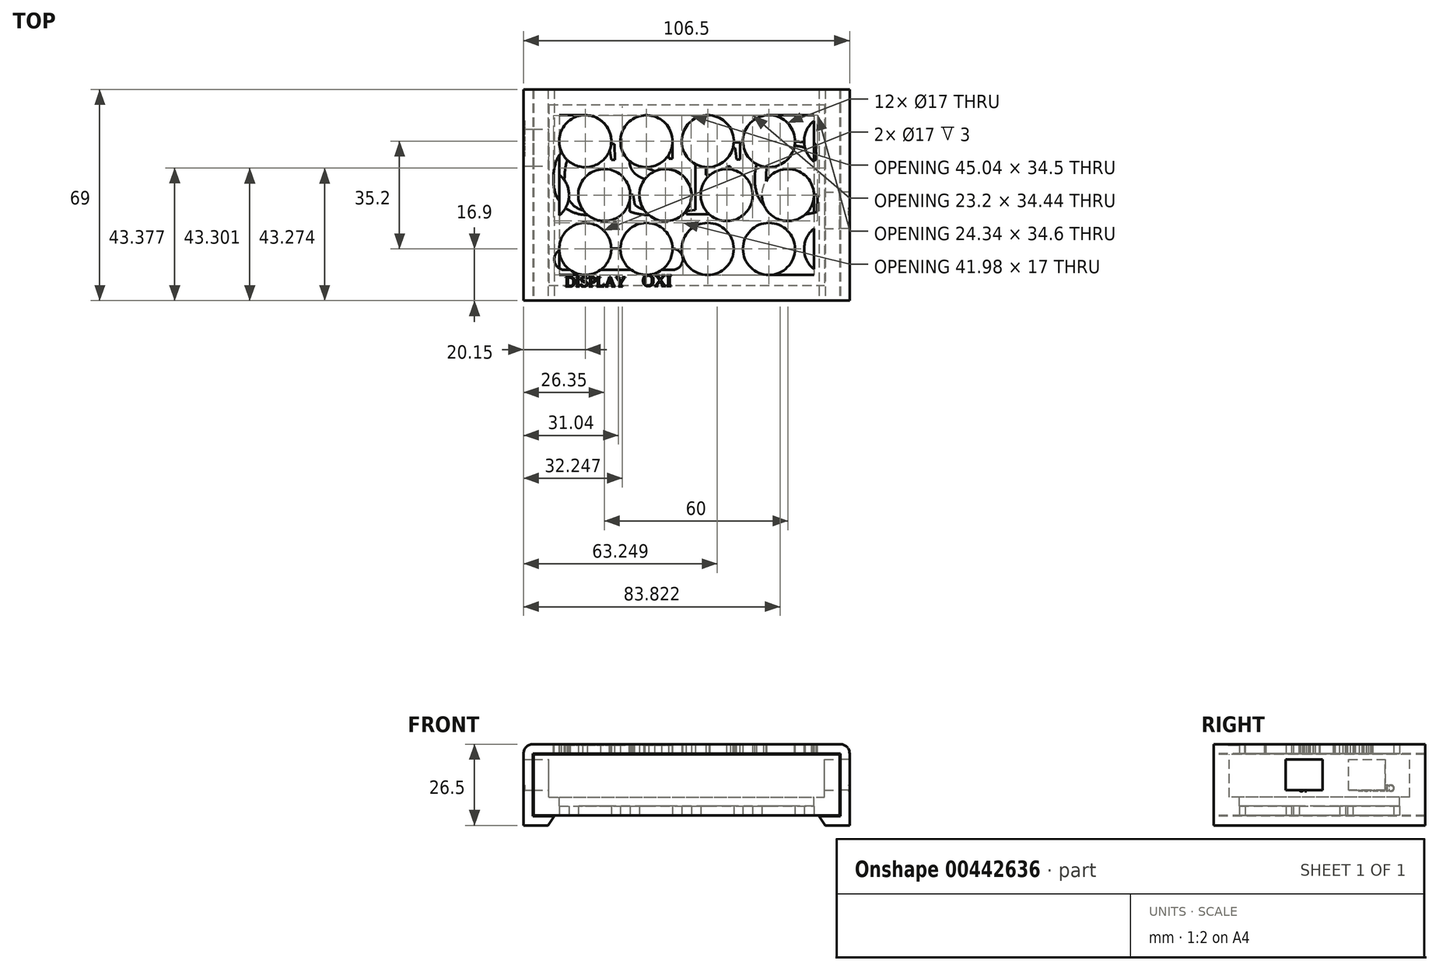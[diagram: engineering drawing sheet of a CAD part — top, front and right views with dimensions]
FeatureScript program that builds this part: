
annotation { "Feature Type Name" : "Feature", "Feature Type Description" : "" }
export const myFeature = defineFeature(function(context is Context, id is Id, definition is map)
    precondition{}
    {
        {
            var Q0;
            Q0=qCreatedBy(makeId("Top.planeOp"),FACE);
            var sketch = newSketch(context, id + "F0", { "sketchPlane" : qUnion([Q0])});
            skLineSegment(sketch, "E0.bottom", {"start": v(-50, 34.5) * mm, "end": v(50, 34.5) * mm});
            skLineSegment(sketch, "E0.top", {"start": v(-50, -34.5) * mm, "end": v(50, -34.5) * mm});
            skLineSegment(sketch, "E0.left", {"start": v(-50, 34.5) * mm, "end": v(-50, -34.5) * mm});
            skLineSegment(sketch, "E0.right", {"start": v(50, 34.5) * mm, "end": v(50, -34.5) * mm});
            skSolve(sketch);
        }
        {
            var Q0;
            Q0=qSketchRegion(id+"F0",true);
            extrude(context, id + "F1", {"entities" : qUnion([Q0]), "depth" : 20 * mm});
        }
        {
            var Q0;
            Q0=makeQuery(id+"F1.opExtrude","CAP_FACE",FACE,{"disambiguationData":[OSD([sQuery(id+"F0.wireOp",EDGE,"E0.bottom"),sQuery(id+"F0.wireOp",EDGE,"E0.top"),sQuery(id+"F0.wireOp",EDGE,"E0.left"),sQuery(id+"F0.wireOp",EDGE,"E0.right")])],"isStart":false});
            var sketch = newSketch(context, id + "F2", { "sketchPlane" : qUnion([Q0])});
            skLineSegment(sketch, "E1.bottom", {"start": v(-45, 29.5) * mm, "end": v(45, 29.5) * mm});
            skLineSegment(sketch, "E1.top", {"start": v(-45, -29.5) * mm, "end": v(45, -29.5) * mm});
            skLineSegment(sketch, "E1.left", {"start": v(-45, 29.5) * mm, "end": v(-45, -29.5) * mm});
            skLineSegment(sketch, "E1.right", {"start": v(45, 29.5) * mm, "end": v(45, -29.5) * mm});
            skSolve(sketch);
        }
        {
            var Q0;
            Q0=makeQuery(id+"F2.imprint","IMPRINT",FACE,{"disambiguationData":[TD([[makeQuery(id+"F2.imprint","IMPRINT",EDGE,{"derivedFrom":sQuery(id+"F2.wireOp",EDGE,"E1.bottom")}),-1.0]])]});
            extrude(context, id + "F3", {"entities" : qUnion([Q0]), "operationType" : NewBodyOperationType.REMOVE, "oppositeDirection" : true, "depth" : 14 * mm});
        }
        {
            var Q0;
            Q0=makeQuery(id+"F3.boolean.opBoolean","COPY",FACE,{"derivedFrom":makeQuery(id+"F3.opExtrude","CAP_FACE",FACE,{"disambiguationData":[OSD([sQuery(id+"F2.wireOp",EDGE,"E1.bottom"),sQuery(id+"F2.wireOp",EDGE,"E1.top"),sQuery(id+"F2.wireOp",EDGE,"E1.left"),sQuery(id+"F2.wireOp",EDGE,"E1.right")])],"isStart":false})});
            var sketch = newSketch(context, id + "F4", { "sketchPlane" : qUnion([Q0])});
            skLineSegment(sketch, "E2.bottom", {"start": v(-41.6, 26.1) * mm, "end": v(41.6, 26.1) * mm});
            skLineSegment(sketch, "E2.top", {"start": v(-41.6, -26.1) * mm, "end": v(41.6, -26.1) * mm});
            skLineSegment(sketch, "E2.left", {"start": v(-41.6, 26.1) * mm, "end": v(-41.6, -26.1) * mm});
            skLineSegment(sketch, "E2.right", {"start": v(41.6, 26.1) * mm, "end": v(41.6, -26.1) * mm});
            skSolve(sketch);
        }
        {
            var Q0;
            Q0=qSketchRegion(id+"F4",true);
            extrude(context, id + "F5", {"entities" : qUnion([Q0]), "operationType" : NewBodyOperationType.REMOVE, "oppositeDirection" : true, "depth" : 3 * mm});
        }
        {
            var Q0;
            Q0=makeQuery(id+"F1.opExtrude","SWEPT_FACE",FACE,{"disambiguationData":[OSD([sQuery(id+"F0.wireOp",EDGE,"E0.top")])]});
            cPlane(context, id + "F6", {"entities" : qUnion([Q0]), "cplaneType" : CPlaneType.OFFSET, "offset" : 0 * mm, "width" : 150 * mm, "height" : 150 * mm});
        }
        {
            var Q0;
            Q0=qCreatedBy(id+"F6.planeOp",FACE);
            var sketch = newSketch(context, id + "F7", { "sketchPlane" : qUnion([Q0])});
            skLineSegment(sketch, "E3.0.0", {"start": v(-50, 0) * mm, "end": v(50, 0) * mm});
            skLineSegment(sketch, "E3.0.1", {"start": v(50, 0) * mm, "end": v(50, 20) * mm});
            skLineSegment(sketch, "E3.0.2", {"start": v(50, 20) * mm, "end": v(-50, 20) * mm});
            skLineSegment(sketch, "E3.0.3", {"start": v(-50, 20) * mm, "end": v(-50, 0) * mm});
            skLineSegment(sketch, "E4", {"start": v(0, 23.25) * mm, "end": v(-53.25, 23.25) * mm});
            skLineSegment(sketch, "E5", {"start": v(-53.25, 23.25) * mm, "end": v(-53.25, -3.25) * mm});
            skLineSegment(sketch, "E6", {"start": v(-53.25, -3.25) * mm, "end": v(-45.25, -3.25) * mm});
            skLineSegment(sketch, "E7", {"start": v(-45.25, -3.25) * mm, "end": v(-43.25, -0.25) * mm});
            skLineSegment(sketch, "E8", {"start": v(-43.25, -0.25) * mm, "end": v(-50.25, -0.25) * mm});
            skLineSegment(sketch, "E9", {"start": v(-50.25, -0.25) * mm, "end": v(-50.25, 20.25) * mm});
            skLineSegment(sketch, "E10", {"start": v(-50.25, 20.25) * mm, "end": v(0, 20.25) * mm});
            skLineSegment(sketch, "E11", {"start": v(0, 20.25) * mm, "end": v(0, 23.25) * mm});
            skLineSegment(sketch, "E12.MirrorCS", {"start": v(0, 23.25) * mm, "end": v(53.25, 23.25) * mm});
            skLineSegment(sketch, "E13.MirrorCS", {"start": v(50.25, 20.25) * mm, "end": v(0, 20.25) * mm});
            skLineSegment(sketch, "E14.MirrorCS", {"start": v(53.25, 23.25) * mm, "end": v(53.25, -3.25) * mm});
            skLineSegment(sketch, "E15.MirrorCS", {"start": v(50.25, -0.25) * mm, "end": v(50.25, 20.25) * mm});
            skLineSegment(sketch, "E16.MirrorCS", {"start": v(53.25, -3.25) * mm, "end": v(45.25, -3.25) * mm});
            skLineSegment(sketch, "E17.MirrorCS", {"start": v(45.25, -3.25) * mm, "end": v(43.25, -0.25) * mm});
            skLineSegment(sketch, "E18.MirrorCS", {"start": v(43.25, -0.25) * mm, "end": v(50.25, -0.25) * mm});
            skSolve(sketch);
        }
        {
            var Q0;
            Q0=makeQuery(id+"F7.imprint","IMPRINT",FACE,{"disambiguationData":[TD([[makeQuery(id+"F7.imprint","IMPRINT",EDGE,{"derivedFrom":sQuery(id+"F7.wireOp",EDGE,"E4")}),1.0]])]});
            var Q1;
            Q1=makeQuery(id+"F7.imprint","IMPRINT",FACE,{"disambiguationData":[TD([[makeQuery(id+"F7.imprint","IMPRINT",EDGE,{"derivedFrom":sQuery(id+"F7.wireOp",EDGE,"E11")}),-1.0]])]});
            extrude(context, id + "F8", {"entities" : qUnion([Q0, Q1]), "oppositeDirection" : true, "depth" : 69 * mm});
        }
        {
            var Q0;
            Q0=makeQuery(id+"F8.opExtrude","SWEPT_FACE",FACE,{"disambiguationData":[OSD([sQuery(id+"F7.wireOp",EDGE,"E4"),sQuery(id+"F7.wireOp",EDGE,"E12.MirrorCS")])]});
            var sketch = newSketch(context, id + "F9", { "sketchPlane" : qUnion([Q0])});
            skLineSegment(sketch, "E19.bottom", {"start": v(-39.7, -17.5) * mm, "end": v(-19.7, -17.5) * mm});
            skLineSegment(sketch, "E19.top", {"start": v(-39.7, -24.5) * mm, "end": v(-19.7, -24.5) * mm});
            skLineSegment(sketch, "E19.left", {"start": v(-39.7, -17.5) * mm, "end": v(-39.7, -24.5) * mm});
            skArc(sketch, "E20", {"start": v(-39.7, -17.5) * mm, "mid": v(-43.2, -21) * mm, "end": v(-39.7, -24.5) * mm});
            skLineSegment(sketch, "E21", {"start": v(-19.7, -17.5) * mm, "end": v(-4.03, -17.5) * mm, "construction": true});
            skLineSegment(sketch, "E22", {"start": v(-19.7, -24.5) * mm, "end": v(-4.03, -24.5) * mm, "construction": true});
            skLineSegment(sketch, "E23.bottom", {"start": v(-14.72, -17.5) * mm, "end": v(-4.72, -17.5) * mm});
            skLineSegment(sketch, "E23.top", {"start": v(-14.45, -24.5) * mm, "end": v(-4.72, -24.5) * mm});
            skLineSegment(sketch, "E23.right", {"start": v(-4.72, -17.5) * mm, "end": v(-4.72, -24.5) * mm});
            skArc(sketch, "E24", {"start": v(-4.72, -24.5) * mm, "mid": v(-1.22, -21) * mm, "end": v(-4.72, -17.5) * mm});
            skText(sketch, "E25", { "text": "DISPLAY", "fontName": "Tinos-Regular.ttf"});
            skText(sketch, "E26", { "text": "OXI", "fontName": "Tinos-Regular.ttf"});
            skLineSegment(sketch, "E27", {"start": v(-19.7, -17.5) * mm, "end": v(-14.45, -17.5) * mm});
            skLineSegment(sketch, "E28", {"start": v(-19.7, -24.5) * mm, "end": v(-14.45, -24.5) * mm});
            const initialGuessF9  = {"E25": [-0.0397, -0.02988, 1, 0, 0.00338], "E26": [-0.01445, -0.02973, 1, 0, 0.00388]};
            skSetInitialGuess(sketch, initialGuessF9);
            skSolve(sketch);
        }
        {
            var Q0;
            Q0=makeQuery(id+"F9.imprint","IMPRINT",FACE,{"disambiguationData":[TD([[makeQuery(id+"F9.imprint","IMPRINT",EDGE,{"derivedFrom":sQuery(id+"F9.wireOp",EDGE,"E23.bottom")}),-1.0]])]});
            var Q1;
            Q1=makeQuery(id+"F9.imprint","IMPRINT",FACE,{"disambiguationData":[TD([[makeQuery(id+"F9.imprint","IMPRINT",EDGE,{"derivedFrom":sQuery(id+"F9.wireOp",EDGE,"E23.left")}),-1.0]])]});
            var Q2;
            Q2=makeQuery(id+"F9.imprint","IMPRINT",FACE,{"disambiguationData":[TD([[makeQuery(id+"F9.imprint","IMPRINT",EDGE,{"derivedFrom":sQuery(id+"F9.wireOp",EDGE,"E23.right")}),1.0]])]});
            var Q3;
            Q3=makeQuery(id+"F9.imprint","IMPRINT",FACE,{"disambiguationData":[TD([[makeQuery(id+"F9.imprint","IMPRINT",EDGE,{"derivedFrom":sQuery(id+"F9.wireOp",EDGE,"E19.right")}),1.0]])]});
            var Q4;
            Q4=makeQuery(id+"F9.imprint","IMPRINT",FACE,{"disambiguationData":[TD([[makeQuery(id+"F9.imprint","IMPRINT",EDGE,{"derivedFrom":sQuery(id+"F9.wireOp",EDGE,"E19.bottom")}),-1.0]])]});
            var Q5;
            Q5=makeQuery(id+"F9.imprint","IMPRINT",FACE,{"disambiguationData":[TD([[makeQuery(id+"F9.imprint","IMPRINT",EDGE,{"derivedFrom":sQuery(id+"F9.wireOp",EDGE,"E19.left")}),-1.0]])]});
            extrude(context, id + "F10", {"entities" : qUnion([Q0, Q1, Q2, Q3, Q4, Q5]), "operationType" : NewBodyOperationType.REMOVE, "oppositeDirection" : true, "depth" : 5 * mm});
        }
        {
            var Q0;
            Q0=makeQuery(id+"F1.opExtrude","CAP_FACE",FACE,{"disambiguationData":[OSD([sQuery(id+"F0.wireOp",EDGE,"E0.bottom"),sQuery(id+"F0.wireOp",EDGE,"E0.top"),sQuery(id+"F0.wireOp",EDGE,"E0.left"),sQuery(id+"F0.wireOp",EDGE,"E0.right")])],"isStart":true});
            var sketch = newSketch(context, id + "F11", { "sketchPlane" : qUnion([Q0])});
            skLineSegment(sketch, "E29.0", {"start": v(-41.6, -26.1) * mm, "end": v(-41.6, 26.1) * mm});
            skLineSegment(sketch, "E30.0", {"start": v(-41.6, -26.1) * mm, "end": v(41.6, -26.1) * mm});
            skLineSegment(sketch, "E31.0", {"start": v(41.6, -26.1) * mm, "end": v(41.6, 26.1) * mm});
            skLineSegment(sketch, "E32.0", {"start": v(-41.6, 26.1) * mm, "end": v(41.6, 26.1) * mm});
            skCircle(sketch, "E33", {"center": v(-33.1, 17.6) * mm, "radius": 8.5 * mm});
            skCircle(sketch, "E34.1.0.0", {"center": v(-13.1, 17.6) * mm, "radius": 8.5 * mm});
            skCircle(sketch, "E34.2.0.0", {"center": v(6.9, 17.6) * mm, "radius": 8.5 * mm});
            skCircle(sketch, "E34.3.0.0", {"center": v(26.9, 17.6) * mm, "radius": 8.5 * mm});
            skArc(sketch, "E34.4.0.0", {"start": v(41.6, 24.25) * mm, "mid": v(38.4, 17.6) * mm, "end": v(41.6, 10.95) * mm});
            skLineSegment(sketch, "E34.direction1", {"start": v(-33.1, 17.6) * mm, "end": v(-13.1, 17.6) * mm, "construction": true});
            skCircle(sketch, "E35", {"center": v(33.1, 0) * mm, "radius": 8.5 * mm});
            skCircle(sketch, "E36.1.0.0", {"center": v(13.1, 0) * mm, "radius": 8.5 * mm});
            skCircle(sketch, "E36.2.0.0", {"center": v(-6.9, 0) * mm, "radius": 8.5 * mm});
            skCircle(sketch, "E36.3.0.0", {"center": v(-26.9, 0) * mm, "radius": 8.5 * mm});
            skArc(sketch, "E36.4.0.0", {"start": v(-41.6, -6.65) * mm, "mid": v(-38.4, 0) * mm, "end": v(-41.6, 6.65) * mm});
            skLineSegment(sketch, "E36.direction1", {"start": v(33.1, 0) * mm, "end": v(13.1, 0) * mm, "construction": true});
            skCircle(sketch, "E37", {"center": v(-33.1, -17.6) * mm, "radius": 8.5 * mm});
            skCircle(sketch, "E38.1.0.0", {"center": v(-13.1, -17.6) * mm, "radius": 8.5 * mm});
            skCircle(sketch, "E38.2.0.0", {"center": v(6.9, -17.6) * mm, "radius": 8.5 * mm});
            skCircle(sketch, "E38.3.0.0", {"center": v(26.9, -17.6) * mm, "radius": 8.5 * mm});
            skArc(sketch, "E38.4.0.0", {"start": v(41.6, -10.95) * mm, "mid": v(38.4, -17.6) * mm, "end": v(41.6, -24.25) * mm});
            skLineSegment(sketch, "E38.direction1", {"start": v(-33.1, -17.6) * mm, "end": v(-13.1, -17.6) * mm, "construction": true});
            skSolve(sketch);
        }
        {
            var Q0;
            Q0=makeQuery(id+"F11.imprint","IMPRINT",FACE,{"disambiguationData":[TD([[makeQuery(id+"F11.imprint","IMPRINT",EDGE,{"derivedFrom":sQuery(id+"F11.wireOp",EDGE,"E34.1.0.0")}),1.0]])]});
            var Q1;
            Q1=makeQuery(id+"F11.imprint","IMPRINT",FACE,{"disambiguationData":[TD([[makeQuery(id+"F11.imprint","IMPRINT",EDGE,{"derivedFrom":sQuery(id+"F11.wireOp",EDGE,"E34.3.0.0")}),1.0]])]});
            var Q2;
            Q2=makeQuery(id+"F11.imprint","IMPRINT",FACE,{"disambiguationData":[TD([[makeQuery(id+"F11.imprint","IMPRINT",EDGE,{"derivedFrom":sQuery(id+"F11.wireOp",EDGE,"E38.1.0.0")}),1.0]])]});
            var Q3;
            Q3=makeQuery(id+"F11.imprint","IMPRINT",FACE,{"disambiguationData":[TD([[makeQuery(id+"F11.imprint","IMPRINT",EDGE,{"derivedFrom":sQuery(id+"F11.wireOp",EDGE,"E38.2.0.0")}),1.0]])]});
            var Q4;
            Q4=makeQuery(id+"F11.imprint","IMPRINT",FACE,{"disambiguationData":[TD([[makeQuery(id+"F11.imprint","IMPRINT",EDGE,{"derivedFrom":sQuery(id+"F11.wireOp",EDGE,"E38.3.0.0")}),1.0]])]});
            var Q5;
            {var subQ0=sQuery(id+"F11.wireOp",EDGE,"E36.4.0.0");Q5=makeQuery(id+"F11.imprint","IMPRINT",FACE,{"disambiguationData":[TD([[makeQuery(id+"F11.imprint","IMPRINT",EDGE,{"derivedFrom":subQ0}),1.0]])]});}
            var Q6;
            {var subQ0=sQuery(id+"F11.wireOp",EDGE,"E38.4.0.0");Q6=makeQuery(id+"F11.imprint","IMPRINT",FACE,{"disambiguationData":[TD([[makeQuery(id+"F11.imprint","IMPRINT",EDGE,{"derivedFrom":subQ0}),1.0]])]});}
            var Q7;
            {var subQ0=sQuery(id+"F11.wireOp",EDGE,"E34.4.0.0");Q7=makeQuery(id+"F11.imprint","IMPRINT",FACE,{"disambiguationData":[TD([[makeQuery(id+"F11.imprint","IMPRINT",EDGE,{"derivedFrom":subQ0}),1.0]])]});}
            var Q8;
            {var subQ0=sQuery(id+"F11.wireOp",EDGE,"E33");var subQ1=makeQuery(id+"F11.imprint","INTERSECT",VERTEX,{"derivedFrom":[sQuery(id+"F11.wireOp",EDGE,"E29.0"),subQ0]});Q8=makeQuery(id+"F11.imprint","IMPRINT",FACE,{"disambiguationData":[TD([[makeQuery(id+"F11.imprint","IMPRINT",EDGE,{"disambiguationData":[TD([[subQ1,1.0]])],"derivedFrom":subQ0}),1.0]])]});}
            var Q9;
            {var subQ0=sQuery(id+"F11.wireOp",EDGE,"E37");var subQ1=makeQuery(id+"F11.imprint","INTERSECT",VERTEX,{"derivedFrom":[sQuery(id+"F11.wireOp",EDGE,"E29.0"),subQ0]});Q9=makeQuery(id+"F11.imprint","IMPRINT",FACE,{"disambiguationData":[TD([[makeQuery(id+"F11.imprint","IMPRINT",EDGE,{"disambiguationData":[TD([[subQ1,-1.0]])],"derivedFrom":subQ0}),1.0]])]});}
            var Q10;
            Q10=makeQuery(id+"F11.imprint","IMPRINT",FACE,{"disambiguationData":[TD([[makeQuery(id+"F11.imprint","IMPRINT",EDGE,{"derivedFrom":sQuery(id+"F11.wireOp",EDGE,"E36.2.0.0")}),1.0]])]});
            var Q11;
            Q11=makeQuery(id+"F11.imprint","IMPRINT",FACE,{"disambiguationData":[TD([[makeQuery(id+"F11.imprint","IMPRINT",EDGE,{"derivedFrom":sQuery(id+"F11.wireOp",EDGE,"E36.1.0.0")}),1.0]])]});
            var Q12;
            Q12=makeQuery(id+"F11.imprint","IMPRINT",FACE,{"disambiguationData":[TD([[makeQuery(id+"F11.imprint","IMPRINT",EDGE,{"derivedFrom":sQuery(id+"F11.wireOp",EDGE,"E36.3.0.0")}),1.0]])]});
            var Q13;
            Q13=makeQuery(id+"F11.imprint","IMPRINT",FACE,{"disambiguationData":[TD([[makeQuery(id+"F11.imprint","IMPRINT",EDGE,{"derivedFrom":sQuery(id+"F11.wireOp",EDGE,"E35")}),1.0]])]});
            var Q14;
            Q14=makeQuery(id+"F11.imprint","IMPRINT",FACE,{"disambiguationData":[TD([[makeQuery(id+"F11.imprint","IMPRINT",EDGE,{"derivedFrom":sQuery(id+"F11.wireOp",EDGE,"E34.2.0.0")}),1.0]])]});
            extrude(context, id + "F12", {"entities" : qUnion([Q0, Q1, Q2, Q3, Q4, Q5, Q6, Q7, Q8, Q9, Q10, Q11, Q12, Q13, Q14]), "operationType" : NewBodyOperationType.REMOVE, "oppositeDirection" : true, "depth" : 25 * mm});
        }
        {
            var Q0;
            Q0=makeQuery(id+"F1.opExtrude","SWEPT_FACE",FACE,{"disambiguationData":[OSD([sQuery(id+"F0.wireOp",EDGE,"E0.right")])]});
            var sketch = newSketch(context, id + "F13", { "sketchPlane" : qUnion([Q0])});
            skLineSegment(sketch, "E39.bottom", {"start": v(-11, 18.25) * mm, "end": v(1, 18.25) * mm});
            skLineSegment(sketch, "E39.top", {"start": v(-11, 8.25) * mm, "end": v(1, 8.25) * mm});
            skLineSegment(sketch, "E39.left", {"start": v(-11, 18.25) * mm, "end": v(-11, 8.25) * mm});
            skLineSegment(sketch, "E39.right", {"start": v(1, 18.25) * mm, "end": v(1, 8.25) * mm});
            skSolve(sketch);
        }
        {
            var Q0;
            Q0=makeQuery(id+"F13.imprint","IMPRINT",FACE,{"disambiguationData":[TD([[makeQuery(id+"F13.imprint","IMPRINT",EDGE,{"derivedFrom":sQuery(id+"F13.wireOp",EDGE,"E39.bottom")}),-1.0]])]});
            extrude(context, id + "F14", {"entities" : qUnion([Q0]), "operationType" : NewBodyOperationType.REMOVE, "depth" : 25 * mm});
        }
        {
            var Q0;
            Q0=makeQuery(id+"F8.opExtrude","SWEPT_FACE",FACE,{"disambiguationData":[OSD([sQuery(id+"F7.wireOp",EDGE,"E4"),sQuery(id+"F7.wireOp",EDGE,"E12.MirrorCS")])]});
            var sketch = newSketch(context, id + "F15", { "sketchPlane" : qUnion([Q0])});
            skText(sketch, "E40", { "text": "CSEC", "fontName": "Tinos-Regular.ttf"});
            const initialGuessF15  = {"E40": [-0.045, -0.00625, 1, 0, 0.02583]};
            skSetInitialGuess(sketch, initialGuessF15);
            skSolve(sketch);
        }
        {
            var Q0;
            Q0=qSketchRegion(id+"F15",true);
            var Q1;
            Q1=makeQuery(id+"F8.opExtrude","SWEPT_FACE",FACE,{"disambiguationData":[OSD([sQuery(id+"F7.wireOp",EDGE,"E10"),sQuery(id+"F7.wireOp",EDGE,"E13.MirrorCS")])]});
            extrude(context, id + "F16", {"entities" : qUnion([Q0]), "operationType" : NewBodyOperationType.REMOVE, "endBound" : BoundingType.UP_TO_SURFACE, "oppositeDirection" : true, "endBoundEntityFace" : qUnion([Q1]), "depth" : 25 * mm});
        }
        {
            var Q0;
            Q0=makeQuery(id+"F13.imprint","IMPRINT",FACE,{"disambiguationData":[TD([[makeQuery(id+"F13.imprint","IMPRINT",EDGE,{"derivedFrom":sQuery(id+"F13.wireOp",EDGE,"E39.bottom")}),-1.0]])]});
            extrude(context, id + "F17", {"entities" : qUnion([Q0]), "operationType" : NewBodyOperationType.REMOVE, "oppositeDirection" : true, "depth" : 25 * mm});
        }
        {
            var Q0;
            Q0=makeQuery(id+"F1.opExtrude","SWEPT_FACE",FACE,{"disambiguationData":[OSD([sQuery(id+"F0.wireOp",EDGE,"E0.left")])]});
            var sketch = newSketch(context, id + "F18", { "sketchPlane" : qUnion([Q0])});
            skLineSegment(sketch, "E41.bottom", {"start": v(-21.5, 18.25) * mm, "end": v(-9.5, 18.25) * mm});
            skLineSegment(sketch, "E41.top", {"start": v(-21.5, 8.25) * mm, "end": v(-9.5, 8.25) * mm});
            skLineSegment(sketch, "E41.left", {"start": v(-21.5, 18.25) * mm, "end": v(-21.5, 8.25) * mm});
            skLineSegment(sketch, "E41.right", {"start": v(-9.5, 18.25) * mm, "end": v(-9.5, 8.25) * mm});
            skSolve(sketch);
        }
        {
            var Q0;
            Q0=makeQuery(id+"F18.imprint","IMPRINT",FACE,{"disambiguationData":[TD([[makeQuery(id+"F18.imprint","IMPRINT",EDGE,{"derivedFrom":sQuery(id+"F18.wireOp",EDGE,"E41.bottom")}),-1.0]])]});
            extrude(context, id + "F19", {"entities" : qUnion([Q0]), "operationType" : NewBodyOperationType.REMOVE, "endBound" : BoundingType.SYMMETRIC, "depth" : 25 * mm});
        }
        {
            var Q0;
            Q0=makeQuery(id+"F8.opExtrude","SWEPT_FACE",FACE,{"disambiguationData":[OSD([sQuery(id+"F7.wireOp",EDGE,"E14.MirrorCS")])]});
            var sketch = newSketch(context, id + "F20", { "sketchPlane" : qUnion([Q0])});
            skText(sketch, "E42", { "text": "UPLOAD", "fontName": "Tinos-Regular.ttf"});
            skLineSegment(sketch, "E43.0.0", {"start": v(34.5, -3.25) * mm, "end": v(34.5, 20.2) * mm});
            skLineSegment(sketch, "E43.0.1", {"start": v(34.5, 20.2) * mm, "end": v(-34.5, 20.2) * mm});
            skLineSegment(sketch, "E43.0.2", {"start": v(-34.5, 20.2) * mm, "end": v(-34.5, -3.25) * mm});
            skLineSegment(sketch, "E43.0.3", {"start": v(-34.5, -3.25) * mm, "end": v(34.5, -3.25) * mm});
            const initialGuessF20  = {"E42": [-0.0125, 0.00793, 1, 0, 0.00212]};
            skSetInitialGuess(sketch, initialGuessF20);
            skSolve(sketch);
        }
        {
            var Q0;
            Q0=makeQuery(id+"F20.imprint","IMPRINT",FACE,{"disambiguationData":[TD([[makeQuery(id+"F20.imprint","IMPRINT",EDGE,{"derivedFrom":sQuery(id+"F20.wireOp",EDGE,"E42.sketch_text.stroke-0")}),-1.0]])]});
            var Q1;
            Q1=makeQuery(id+"F20.imprint","IMPRINT",FACE,{"disambiguationData":[TD([[makeQuery(id+"F20.imprint","IMPRINT",EDGE,{"derivedFrom":sQuery(id+"F20.wireOp",EDGE,"E42.sketch_text.stroke-21")}),-1.0]])]});
            var Q2;
            Q2=makeQuery(id+"F20.imprint","IMPRINT",FACE,{"disambiguationData":[TD([[makeQuery(id+"F20.imprint","IMPRINT",EDGE,{"derivedFrom":sQuery(id+"F20.wireOp",EDGE,"E42.sketch_text.stroke-42")}),-1.0]])]});
            var Q3;
            Q3=makeQuery(id+"F20.imprint","IMPRINT",FACE,{"disambiguationData":[TD([[makeQuery(id+"F20.imprint","IMPRINT",EDGE,{"derivedFrom":sQuery(id+"F20.wireOp",EDGE,"E42.sketch_text.stroke-57")}),-1.0]])]});
            var Q4;
            Q4=makeQuery(id+"F20.imprint","IMPRINT",FACE,{"disambiguationData":[TD([[makeQuery(id+"F20.imprint","IMPRINT",EDGE,{"derivedFrom":sQuery(id+"F20.wireOp",EDGE,"E42.sketch_text.stroke-72")}),-1.0]])]});
            var Q5;
            Q5=makeQuery(id+"F20.imprint","IMPRINT",FACE,{"disambiguationData":[TD([[makeQuery(id+"F20.imprint","IMPRINT",EDGE,{"derivedFrom":sQuery(id+"F20.wireOp",EDGE,"E42.sketch_text.stroke-91")}),-1.0]])]});
            extrude(context, id + "F21", {"entities" : qUnion([Q0, Q1, Q2, Q3, Q4, Q5]), "operationType" : NewBodyOperationType.REMOVE, "oppositeDirection" : true, "depth" : 0.4 * mm});
        }
        {
            var Q0;
            Q0=makeQuery(id+"F8.opExtrude","SWEPT_FACE",FACE,{"disambiguationData":[OSD([sQuery(id+"F7.wireOp",EDGE,"E5")])]});
            var sketch = newSketch(context, id + "F22", { "sketchPlane" : qUnion([Q0])});
            skText(sketch, "E44", { "text": "CHARGE", "fontName": "Tinos-Regular.ttf"});
            const initialGuessF22  = {"E44": [-0.0245, 0.00796, 1, 0, 0.0021]};
            skSetInitialGuess(sketch, initialGuessF22);
            skSolve(sketch);
        }
        {
            var Q0;
            Q0=qSketchRegion(id+"F22",true);
            extrude(context, id + "F23", {"entities" : qUnion([Q0]), "operationType" : NewBodyOperationType.REMOVE, "oppositeDirection" : true, "depth" : 0.4 * mm});
        }
        {
            var Q0;
            Q0=makeQuery(id+"F8.opExtrude","SWEPT_EDGE",EDGE,{"disambiguationData":[OSD([sQuery(id+"F7.wireOp",EDGE,"E4"),sQuery(id+"F7.wireOp",EDGE,"E5")])]});
            var Q1;
            Q1=makeQuery(id+"F8.opExtrude","SWEPT_EDGE",EDGE,{"disambiguationData":[OSD([sQuery(id+"F7.wireOp",EDGE,"E12.MirrorCS"),sQuery(id+"F7.wireOp",EDGE,"E14.MirrorCS")])]});
            fillet(context, id + "F24", {"entities" : qUnion([Q0, Q1]), "radius" : 3 * mm, "tangentPropagation" : true, "allowEdgeOverflow" : false});
        }
        {
            var Q0;
            Q0=makeQuery(id+"F9.imprint","IMPRINT",FACE,{"disambiguationData":[TD([[makeQuery(id+"F9.imprint","IMPRINT",EDGE,{"derivedFrom":sQuery(id+"F9.wireOp",EDGE,"E25.sketch_text.stroke-0")}),-1.0]])]});
            var Q1;
            Q1=makeQuery(id+"F9.imprint","IMPRINT",FACE,{"disambiguationData":[TD([[makeQuery(id+"F9.imprint","IMPRINT",EDGE,{"derivedFrom":sQuery(id+"F9.wireOp",EDGE,"E25.sketch_text.stroke-19")}),-1.0]])]});
            var Q2;
            Q2=makeQuery(id+"F9.imprint","IMPRINT",FACE,{"disambiguationData":[TD([[makeQuery(id+"F9.imprint","IMPRINT",EDGE,{"derivedFrom":sQuery(id+"F9.wireOp",EDGE,"E25.sketch_text.stroke-31")}),-1.0]])]});
            var Q3;
            Q3=makeQuery(id+"F9.imprint","IMPRINT",FACE,{"disambiguationData":[TD([[makeQuery(id+"F9.imprint","IMPRINT",EDGE,{"derivedFrom":sQuery(id+"F9.wireOp",EDGE,"E25.sketch_text.stroke-67")}),-1.0]])]});
            var Q4;
            Q4=makeQuery(id+"F9.imprint","IMPRINT",FACE,{"disambiguationData":[TD([[makeQuery(id+"F9.imprint","IMPRINT",EDGE,{"derivedFrom":sQuery(id+"F9.wireOp",EDGE,"E25.sketch_text.stroke-88")}),-1.0]])]});
            var Q5;
            Q5=makeQuery(id+"F9.imprint","IMPRINT",FACE,{"disambiguationData":[TD([[makeQuery(id+"F9.imprint","IMPRINT",EDGE,{"derivedFrom":sQuery(id+"F9.wireOp",EDGE,"E25.sketch_text.stroke-103")}),-1.0]])]});
            var Q6;
            Q6=makeQuery(id+"F9.imprint","IMPRINT",FACE,{"disambiguationData":[TD([[makeQuery(id+"F9.imprint","IMPRINT",EDGE,{"derivedFrom":sQuery(id+"F9.wireOp",EDGE,"E25.sketch_text.stroke-122")}),-1.0]])]});
            var Q7;
            Q7=makeQuery(id+"F9.imprint","IMPRINT",FACE,{"disambiguationData":[TD([[makeQuery(id+"F9.imprint","IMPRINT",EDGE,{"derivedFrom":sQuery(id+"F9.wireOp",EDGE,"E26.sketch_text.stroke-0")}),-1.0]])]});
            var Q8;
            Q8=makeQuery(id+"F9.imprint","IMPRINT",FACE,{"disambiguationData":[TD([[makeQuery(id+"F9.imprint","IMPRINT",EDGE,{"derivedFrom":sQuery(id+"F9.wireOp",EDGE,"E26.sketch_text.stroke-15")}),-1.0]])]});
            var Q9;
            Q9=makeQuery(id+"F9.imprint","IMPRINT",FACE,{"disambiguationData":[TD([[makeQuery(id+"F9.imprint","IMPRINT",EDGE,{"derivedFrom":sQuery(id+"F9.wireOp",EDGE,"E26.sketch_text.stroke-43")}),-1.0]])]});
            extrude(context, id + "F25", {"entities" : qUnion([Q0, Q1, Q2, Q3, Q4, Q5, Q6, Q7, Q8, Q9]), "operationType" : NewBodyOperationType.REMOVE, "oppositeDirection" : true, "depth" : 0.3 * mm});
        }
    });
